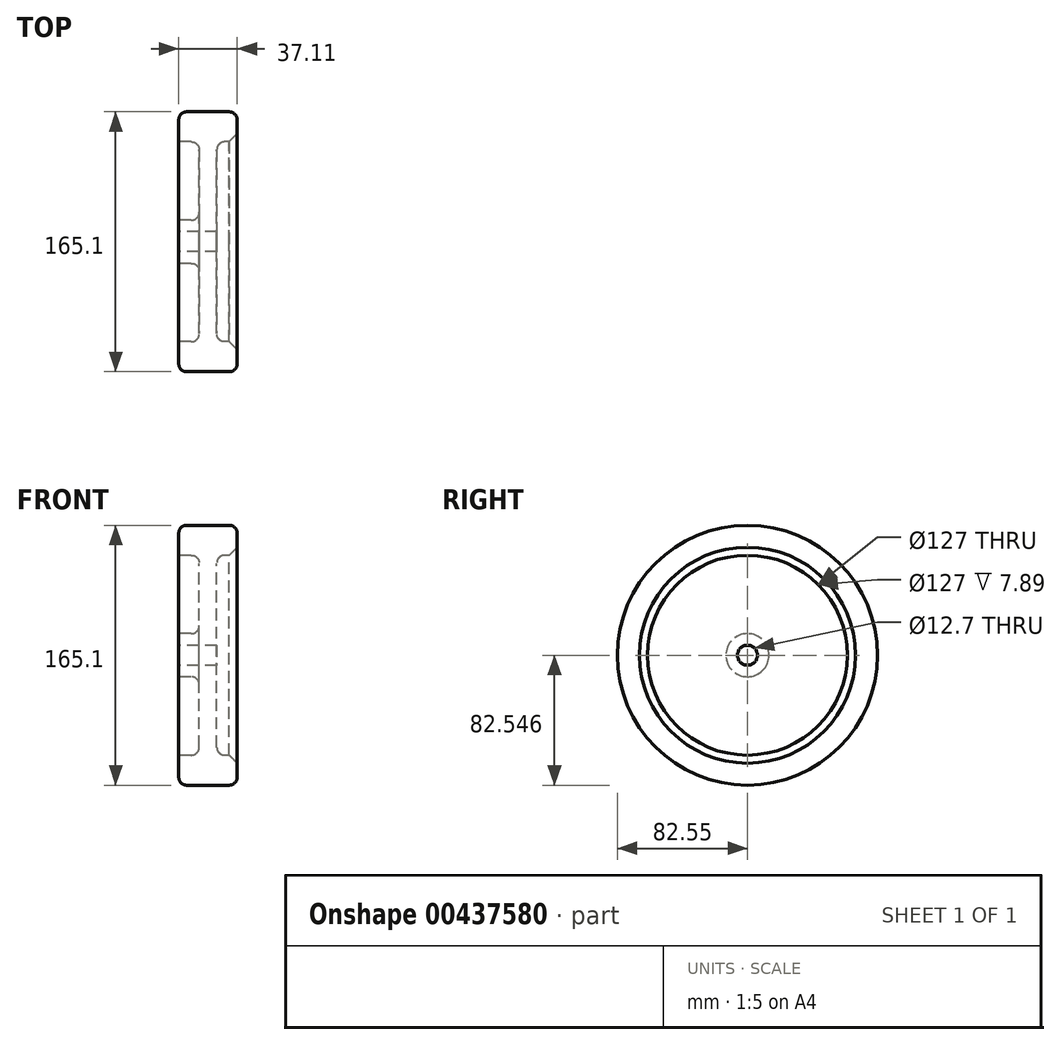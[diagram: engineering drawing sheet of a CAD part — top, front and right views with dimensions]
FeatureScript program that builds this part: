
annotation { "Feature Type Name" : "Feature", "Feature Type Description" : "" }
export const myFeature = defineFeature(function(context is Context, id is Id, definition is map)
    precondition{}
    {
        {
            var Q0;
            Q0=qCreatedBy(makeId("Front.planeOp"),FACE);
            var sketch = newSketch(context, id + "F0", { "sketchPlane" : qUnion([Q0])});
            skLineSegment(sketch, "E0.bottom", {"start": v(-17.7, 62.2) * mm, "end": v(19.4, 62.2) * mm});
            skLineSegment(sketch, "E0.top", {"start": v(-17.7, 43.15) * mm, "end": v(-4.73, 43.15) * mm});
            skLineSegment(sketch, "E0.left", {"start": v(-17.7, 62.2) * mm, "end": v(-17.7, 43.15) * mm});
            skLineSegment(sketch, "E0.right", {"start": v(19.4, 62.2) * mm, "end": v(19.4, 43.15) * mm});
            skLineSegment(sketch, "E1.top", {"start": v(-4.73, -14) * mm, "end": v(6.44, -14) * mm});
            skLineSegment(sketch, "E1.left", {"start": v(-4.73, 43.15) * mm, "end": v(-4.73, -6.67) * mm});
            skLineSegment(sketch, "E1.right", {"start": v(6.44, 43.15) * mm, "end": v(6.44, -14) * mm});
            skLineSegment(sketch, "E2.trimOffspring", {"start": v(6.44, 43.15) * mm, "end": v(19.4, 43.15) * mm});
            skLineSegment(sketch, "E3", {"start": v(-4.52, -20.35) * mm, "end": v(18.19, -20.35) * mm});
            skLineSegment(sketch, "E4", {"start": v(-17.7, -6.67) * mm, "end": v(-17.7, -14) * mm});
            skLineSegment(sketch, "E5", {"start": v(-4.73, -14) * mm, "end": v(-17.7, -14) * mm});
            skLineSegment(sketch, "E6", {"start": v(-4.73, -6.67) * mm, "end": v(-17.7, -6.67) * mm});
            skSolve(sketch);
        }
        {
            var Q0;
            Q0=makeQuery(id+"F0.imprint","IMPRINT",FACE,{"disambiguationData":[TD([[makeQuery(id+"F0.imprint","IMPRINT",EDGE,{"derivedFrom":sQuery(id+"F0.wireOp",EDGE,"E0.bottom")}),-1.0]])]});
            var Q1;
            Q1=sQuery(id+"F0.wireOp",EDGE,"E3");
            revolve(context, id + "F1", {"entities" : qUnion([Q0]), "axis" : qUnion([Q1]), "revolveType" : RevolveType.FULL});
        }
        {
            var Q0;
            Q0=makeQuery(id+"F1.opRevolve","SWEPT_EDGE",EDGE,{"disambiguationData":[OSD([sQuery(id+"F0.wireOp",EDGE,"E0.top"),sQuery(id+"F0.wireOp",EDGE,"E1.left")])]});
            var Q1;
            Q1=makeQuery(id+"F1.opRevolve","SWEPT_EDGE",EDGE,{"disambiguationData":[OSD([sQuery(id+"F0.wireOp",EDGE,"E1.right"),sQuery(id+"F0.wireOp",EDGE,"E2.trimOffspring")])]});
            var Q2;
            Q2=makeQuery(id+"F1.opRevolve","SWEPT_EDGE",EDGE,{"disambiguationData":[OSD([sQuery(id+"F0.wireOp",EDGE,"E0.bottom"),sQuery(id+"F0.wireOp",EDGE,"E0.right")])]});
            var Q3;
            Q3=makeQuery(id+"F1.opRevolve","SWEPT_EDGE",EDGE,{"disambiguationData":[OSD([sQuery(id+"F0.wireOp",EDGE,"E0.bottom"),sQuery(id+"F0.wireOp",EDGE,"E0.left")])]});
            fillet(context, id + "F2", {"entities" : qUnion([Q0, Q1, Q2, Q3]), "radius" : 5.08 * mm, "tangentPropagation" : true, "allowEdgeOverflow" : false});
        }
        {
            var Q0;
            Q0=makeQuery(id+"F1.opRevolve","SWEPT_EDGE",EDGE,{"disambiguationData":[OSD([sQuery(id+"F0.wireOp",EDGE,"E0.right"),sQuery(id+"F0.wireOp",EDGE,"E2.trimOffspring")])]});
            chamfer(context, id + "F3", {"entities" : qUnion([Q0]), "width" : 5.08 * mm, "tangentPropagation" : true});
        }
        {
            var Q0;
            Q0=makeQuery(id+"F1.opRevolve","SWEPT_EDGE",EDGE,{"disambiguationData":[OSD([sQuery(id+"F0.wireOp",EDGE,"E1.left"),sQuery(id+"F0.wireOp",EDGE,"E6")])]});
            fillet(context, id + "F4", {"entities" : qUnion([Q0]), "radius" : 5.08 * mm, "tangentPropagation" : true, "allowEdgeOverflow" : false});
        }
    });
